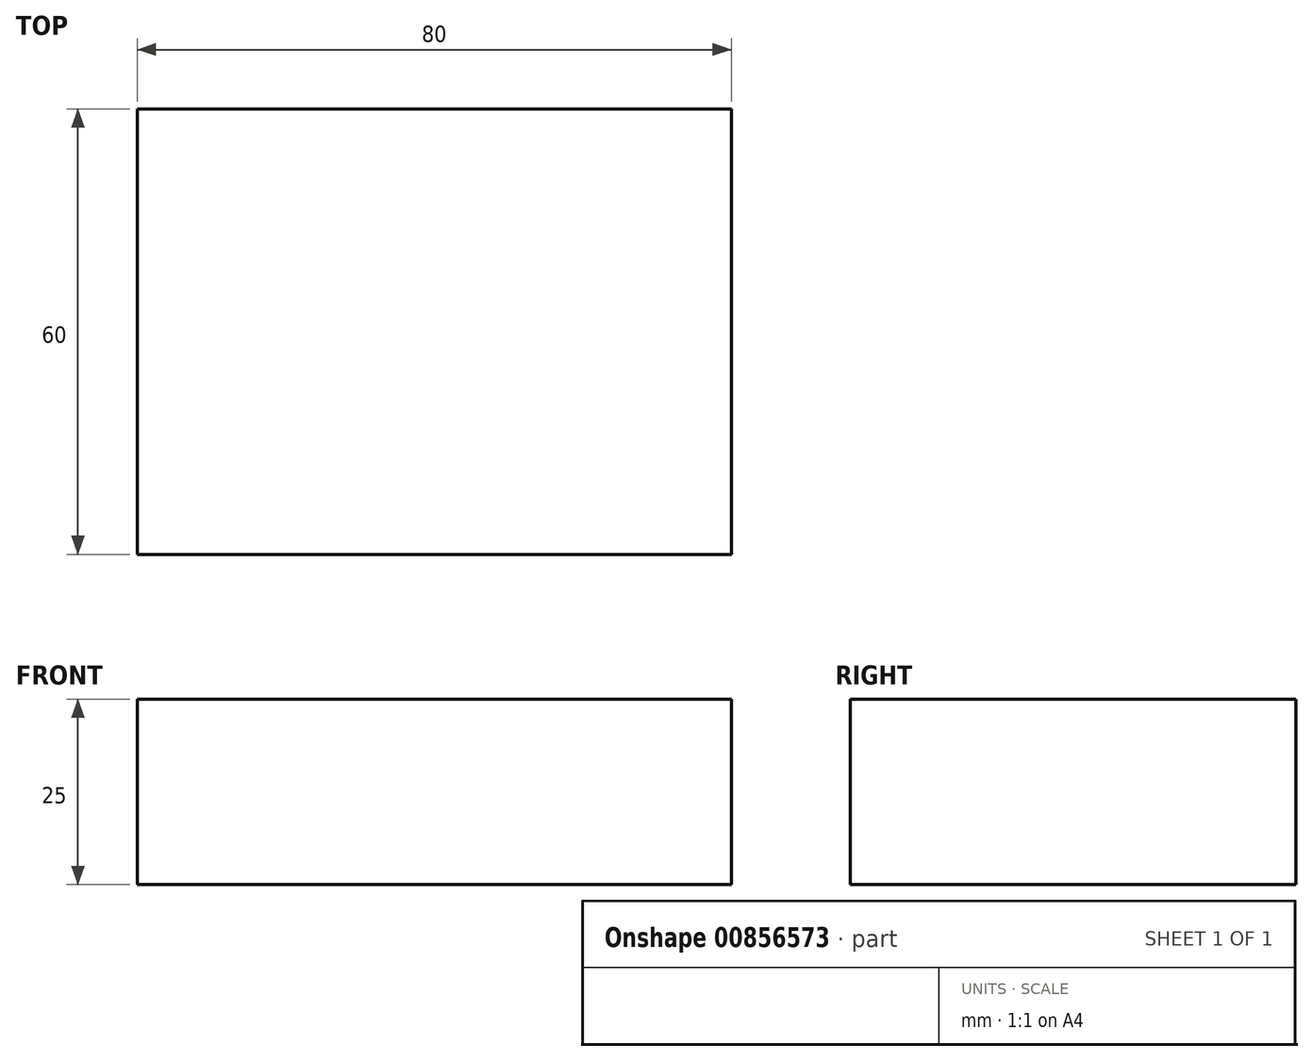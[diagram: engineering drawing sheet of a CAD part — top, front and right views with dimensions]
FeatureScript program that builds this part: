
annotation { "Feature Type Name" : "Feature", "Feature Type Description" : "" }
export const myFeature = defineFeature(function(context is Context, id is Id, definition is map)
    precondition{}
    {
        {
            var Q0;
            Q0=qCreatedBy(makeId("Top.planeOp"),FACE);
            var sketch = newSketch(context, id + "F0", { "sketchPlane" : qUnion([Q0])});
            skLineSegment(sketch, "E0.bottom", {"start": v(-39.33, 48.68) * mm, "end": v(40.67, 48.68) * mm});
            skLineSegment(sketch, "E0.top", {"start": v(-39.33, -11.32) * mm, "end": v(40.67, -11.32) * mm});
            skLineSegment(sketch, "E0.left", {"start": v(-39.33, 48.68) * mm, "end": v(-39.33, -11.32) * mm});
            skLineSegment(sketch, "E0.right", {"start": v(40.67, 48.68) * mm, "end": v(40.67, -11.32) * mm});
            skSolve(sketch);
        }
        {
            var Q0;
            Q0=makeQuery(id+"F0.imprint","IMPRINT",FACE,{"disambiguationData":[TD([[makeQuery(id+"F0.imprint","IMPRINT",EDGE,{"derivedFrom":sQuery(id+"F0.wireOp",EDGE,"E0.bottom")}),-1.0]])]});
            extrude(context, id + "F1", {"entities" : qUnion([Q0]), "depth" : 25 * mm, "offsetDistance" : 25 * mm});
        }
    });
